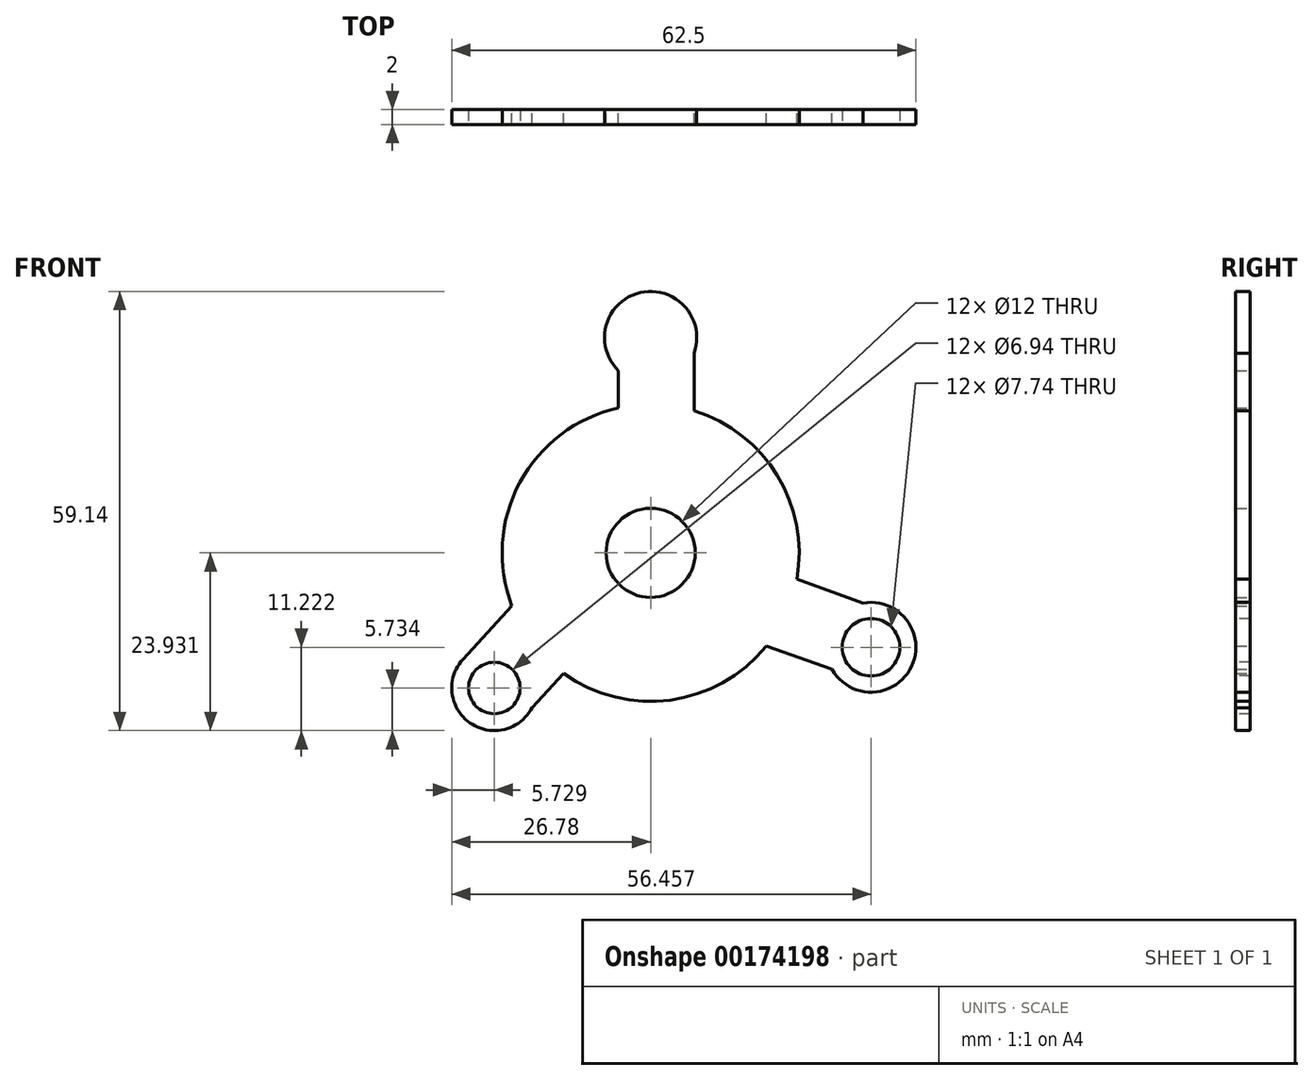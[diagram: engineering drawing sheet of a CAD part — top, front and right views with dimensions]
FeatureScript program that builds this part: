
annotation { "Feature Type Name" : "Feature", "Feature Type Description" : "" }
export const myFeature = defineFeature(function(context is Context, id is Id, definition is map)
    precondition{}
    {
        {
            var Q0;
            Q0=qCreatedBy(makeId("Front.planeOp"),FACE);
            var sketch = newSketch(context, id + "F0", { "sketchPlane" : qUnion([Q0])});
            skCircle(sketch, "E0", {"center": v(0, 23.36) * mm, "radius": 20 * mm});
            skCircle(sketch, "E1", {"center": v(0, 23.36) * mm, "radius": 6 * mm});
            skLineSegment(sketch, "E2", {"start": v(-4.33, 42.89) * mm, "end": v(-4.33, 52.36) * mm});
            skLineSegment(sketch, "E3", {"start": v(5.85, 52.36) * mm, "end": v(5.85, 42.49) * mm});
            skLineSegment(sketch, "E4", {"start": v(19.68, 19.8) * mm, "end": v(29.68, 16.21) * mm});
            skLineSegment(sketch, "E5", {"start": v(15.57, 10.8) * mm, "end": v(26.1, 7.08) * mm});
            skLineSegment(sketch, "E6", {"start": v(-18.68, 16.21) * mm, "end": v(-27, 7.15) * mm});
            skLineSegment(sketch, "E7", {"start": v(-11.71, 7.15) * mm, "end": v(-17, 1.4) * mm});
            skArc(sketch, "E8", {"start": v(5.85, 50.24) * mm, "mid": v(-1.4, 58.41) * mm, "end": v(-4.33, 47.9) * mm});
            skPoint(sketch, "E9.center.orphan", {"position": v(29.68, 10.65) * mm});
            skArc(sketch, "E10", {"start": v(24.42, 7.67) * mm, "mid": v(35.15, 8.09) * mm, "end": v(28.6, 16.6) * mm});
            skArc(sketch, "E11", {"start": v(-25.27, 9.04) * mm, "mid": v(-24.34, 0.47) * mm, "end": v(-15.97, 2.52) * mm});
            skSolve(sketch);
        }
        {
            var Q0;
            Q0=sQuery(id+"F0.wireOp",EDGE,"E1");
            extrude(context, id + "F1", {"bodyType" : ToolBodyType.SURFACE, "surfaceEntities" : qUnion([Q0]), "depth" : 2 * mm});
        }
        {
            var Q0;
            Q0=sQuery(id+"F0.wireOp",EDGE,"E0");
            extrude(context, id + "F2", {"bodyType" : ToolBodyType.SURFACE, "surfaceEntities" : qUnion([Q0]), "depth" : 5 * mm});
        }
        {
            var Q0;
            Q0 = qSketchRegion(id + "F0", true);
            extrude(context, id + "F3", {"entities" : qUnion([Q0]), "depth" : 2 * mm});
        }
        {
            var Q0;
            Q0=qCreatedBy(makeId("Front.planeOp"),FACE);
            var sketch = newSketch(context, id + "F4", { "sketchPlane" : qUnion([Q0])});
            skCircle(sketch, "E12", {"center": v(0, 53.64) * mm, "radius": 2.94 * mm});
            skCircle(sketch, "E13", {"center": v(29.5, 10.31) * mm, "radius": 2.96 * mm});
            skCircle(sketch, "E14", {"center": v(-20.8, 4.8) * mm, "radius": 3.14 * mm});
            skSolve(sketch);
        }
        {
            var Q0;
            Q0 = qSketchRegion(id + "F4", true);
            extrude(context, id + "F5", {"entities" : qUnion([Q0]), "operationType" : NewBodyOperationType.REMOVE, "oppositeDirection" : true, "depth" : 25 * mm});
        }
        {
            var Q0;
            Q0=makeQuery(id+"F3.opExtrude","CAP_FACE",FACE,{"disambiguationData":[OSD([sQuery(id+"F0.wireOp",EDGE,"E0"),sQuery(id+"F0.wireOp",EDGE,"E1"),sQuery(id+"F0.wireOp",EDGE,"E2"),sQuery(id+"F0.wireOp",EDGE,"E3"),sQuery(id+"F0.wireOp",EDGE,"E4"),sQuery(id+"F0.wireOp",EDGE,"E5"),sQuery(id+"F0.wireOp",EDGE,"E6"),sQuery(id+"F0.wireOp",EDGE,"E7"),sQuery(id+"F0.wireOp",EDGE,"E8"),sQuery(id+"F0.wireOp",EDGE,"E10"),sQuery(id+"F0.wireOp",EDGE,"E11")])],"isStart":false});
            var sketch = newSketch(context, id + "F6", { "sketchPlane" : qUnion([Q0])});
            skCircle(sketch, "E15", {"center": v(0, 52.36) * mm, "radius": 3.48 * mm});
            skCircle(sketch, "E16", {"center": v(29.68, 10.65) * mm, "radius": 3.87 * mm});
            skCircle(sketch, "E17", {"center": v(-21.05, 5.16) * mm, "radius": 3.47 * mm});
            skSolve(sketch);
        }
        {
            var Q0;
            Q0=makeQuery(id+"F6.imprint","IMPRINT",FACE,{"disambiguationData":[TD([[makeQuery(id+"F6.imprint","IMPRINT",EDGE,{"derivedFrom":sQuery(id+"F6.wireOp",EDGE,"E16")}),1.0]])]});
            var Q1;
            Q1=makeQuery(id+"F6.imprint","IMPRINT",FACE,{"disambiguationData":[TD([[makeQuery(id+"F6.imprint","IMPRINT",EDGE,{"derivedFrom":sQuery(id+"F6.wireOp",EDGE,"E17")}),1.0]])]});
            extrude(context, id + "F7", {"entities" : qUnion([Q0, Q1]), "operationType" : NewBodyOperationType.REMOVE, "oppositeDirection" : true, "depth" : 3 * mm});
        }
    });
